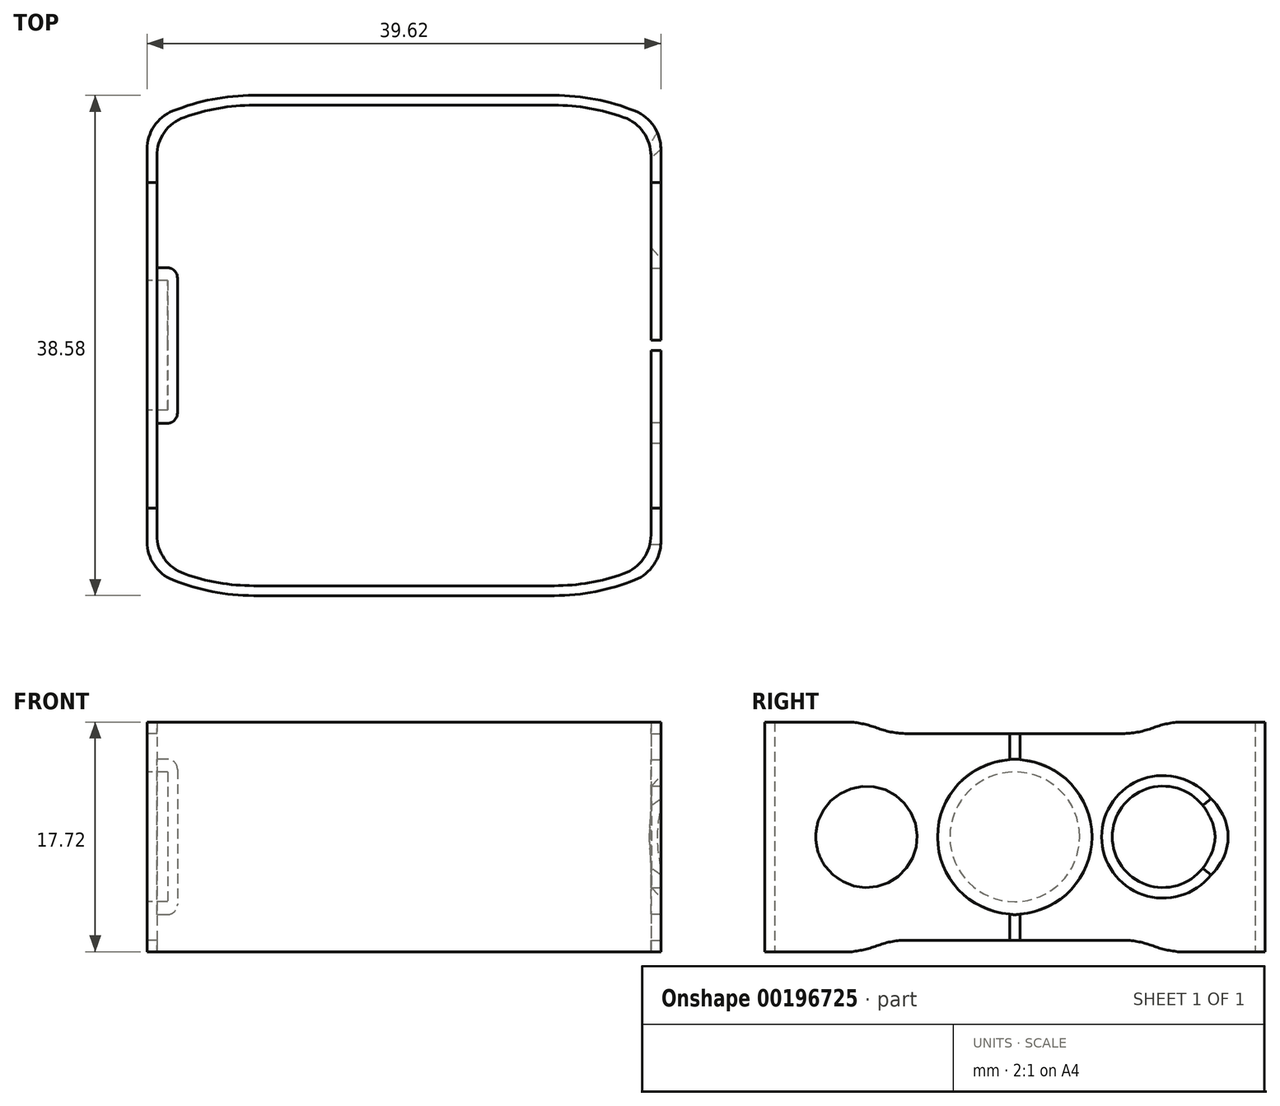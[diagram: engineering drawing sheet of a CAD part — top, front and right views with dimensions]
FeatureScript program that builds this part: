
annotation { "Feature Type Name" : "Feature", "Feature Type Description" : "" }
export const myFeature = defineFeature(function(context is Context, id is Id, definition is map)
    precondition{}
    {
        {
            var Q0;
            Q0=qCreatedBy(makeId("Top.planeOp"),FACE);
            var sketch = newSketch(context, id + "F0", { "sketchPlane" : qUnion([Q0])});
            skLineSegment(sketch, "E0.bottom", {"start": v(19.05, 16.67) * mm, "end": v(-19.05, 16.67) * mm});
            skLineSegment(sketch, "E0.top", {"start": v(19.05, -16.67) * mm, "end": v(-19.05, -16.67) * mm});
            skLineSegment(sketch, "E0.left", {"start": v(19.05, 14.61) * mm, "end": v(19.05, -14.61) * mm});
            skLineSegment(sketch, "E0.right", {"start": v(-19.05, 14.61) * mm, "end": v(-19.05, -14.61) * mm});
            skPoint(sketch, "E0.middle", {"position": v(0, 0) * mm});
            skLineSegment(sketch, "E1", {"start": v(-29.61, 0) * mm, "end": v(26.31, 0) * mm, "construction": true});
            skPoint(sketch, "E1.startSnap0", {"position": v(-19.05, 0) * mm});
            skLineSegment(sketch, "E2", {"start": v(-11.59, 18.53) * mm, "end": v(0, 18.53) * mm});
            skLineSegment(sketch, "E3", {"start": v(0, 18.53) * mm, "end": v(11.59, 18.53) * mm});
            skArc(sketch, "E4", {"start": v(-11.59, 18.53) * mm, "mid": v(-14.3, 18.3) * mm, "end": v(-16.95, 17.6) * mm});
            skArc(sketch, "E5", {"start": v(16.95, 17.6) * mm, "mid": v(14.3, 18.3) * mm, "end": v(11.59, 18.53) * mm});
            skArc(sketch, "E6.MirrorCS", {"start": v(-11.59, -18.53) * mm, "mid": v(-14.3, -18.3) * mm, "end": v(-16.95, -17.6) * mm});
            skLineSegment(sketch, "E7.MirrorCS", {"start": v(-11.59, -18.53) * mm, "end": v(0, -18.53) * mm});
            skLineSegment(sketch, "E8.MirrorCS", {"start": v(0, -18.53) * mm, "end": v(11.59, -18.53) * mm});
            skArc(sketch, "E9.MirrorCS", {"start": v(16.95, -17.6) * mm, "mid": v(14.3, -18.3) * mm, "end": v(11.59, -18.53) * mm});
            skLineSegment(sketch, "E10.0", {"start": v(-11.59, 19.3) * mm, "end": v(0, 19.3) * mm});
            skLineSegment(sketch, "E10.1", {"start": v(0, 19.3) * mm, "end": v(11.59, 19.3) * mm});
            skArc(sketch, "E10.2", {"start": v(-11.59, 19.3) * mm, "mid": v(-14.77, 18.99) * mm, "end": v(-17.83, 18.08) * mm});
            skArc(sketch, "E10.3", {"start": v(17.83, 18.08) * mm, "mid": v(14.77, 18.99) * mm, "end": v(11.59, 19.3) * mm});
            skLineSegment(sketch, "E10.4", {"start": v(19.81, 15.14) * mm, "end": v(19.81, -15.14) * mm});
            skArc(sketch, "E10.5", {"start": v(17.83, -18.08) * mm, "mid": v(14.77, -18.99) * mm, "end": v(11.59, -19.3) * mm});
            skLineSegment(sketch, "E10.6", {"start": v(-19.81, 15.14) * mm, "end": v(-19.81, -15.14) * mm});
            skArc(sketch, "E10.7", {"start": v(-11.59, -19.3) * mm, "mid": v(-14.77, -18.99) * mm, "end": v(-17.83, -18.08) * mm});
            skLineSegment(sketch, "E10.8", {"start": v(-11.59, -19.3) * mm, "end": v(0, -19.3) * mm});
            skLineSegment(sketch, "E10.9", {"start": v(0, -19.3) * mm, "end": v(11.59, -19.3) * mm});
            skPoint(sketch, "E11.visualSharp", {"position": v(-19.05, 16.67) * mm});
            skArc(sketch, "E11.filletArc", {"start": v(-16.95, 17.6) * mm, "mid": v(-18.47, 16.44) * mm, "end": v(-19.05, 14.61) * mm});
            skPoint(sketch, "E12.visualSharp", {"position": v(-19.81, 17.12) * mm});
            skArc(sketch, "E12.filletArc", {"start": v(-17.83, 18.08) * mm, "mid": v(-19.27, 16.91) * mm, "end": v(-19.81, 15.14) * mm});
            skPoint(sketch, "E13.visualSharp", {"position": v(19.05, 16.67) * mm});
            skArc(sketch, "E13.filletArc", {"start": v(19.05, 14.61) * mm, "mid": v(18.47, 16.44) * mm, "end": v(16.95, 17.6) * mm});
            skPoint(sketch, "E14.visualSharp", {"position": v(19.81, 17.12) * mm});
            skArc(sketch, "E14.filletArc", {"start": v(19.81, 15.14) * mm, "mid": v(19.27, 16.91) * mm, "end": v(17.83, 18.08) * mm});
            skPoint(sketch, "E15.visualSharp", {"position": v(19.05, -16.67) * mm});
            skArc(sketch, "E15.filletArc", {"start": v(16.95, -17.6) * mm, "mid": v(18.47, -16.44) * mm, "end": v(19.05, -14.61) * mm});
            skPoint(sketch, "E16.visualSharp", {"position": v(19.81, -17.12) * mm});
            skArc(sketch, "E16.filletArc", {"start": v(17.83, -18.08) * mm, "mid": v(19.27, -16.91) * mm, "end": v(19.81, -15.14) * mm});
            skPoint(sketch, "E17.visualSharp", {"position": v(-19.05, -16.67) * mm});
            skArc(sketch, "E17.filletArc", {"start": v(-19.05, -14.61) * mm, "mid": v(-18.47, -16.44) * mm, "end": v(-16.95, -17.6) * mm});
            skPoint(sketch, "E18.visualSharp", {"position": v(-19.81, -17.12) * mm});
            skArc(sketch, "E18.filletArc", {"start": v(-19.81, -15.14) * mm, "mid": v(-19.27, -16.91) * mm, "end": v(-17.83, -18.08) * mm});
            skSolve(sketch);
        }
        {
            var Q0;
            Q0=makeQuery(id+"F0.imprint","IMPRINT",FACE,{"disambiguationData":[TD([[makeQuery(id+"F0.imprint","IMPRINT",EDGE,{"derivedFrom":sQuery(id+"F0.wireOp",EDGE,"E0.left")}),1.0]])]});
            extrude(context, id + "F1", {"entities" : qUnion([Q0]), "endBound" : BoundingType.SYMMETRIC, "depth" : 17.72 * mm});
        }
        {
            var Q0;
            Q0=makeQuery(id+"F1.opExtrude","SWEPT_FACE",FACE,{"disambiguationData":[OSD([sQuery(id+"F0.wireOp",EDGE,"E10.4")])]});
            var sketch = newSketch(context, id + "F2", { "sketchPlane" : qUnion([Q0])});
            skCircle(sketch, "E19", {"center": v(0, 0) * mm, "radius": 5.95 * mm});
            skLineSegment(sketch, "E20.bottom", {"start": v(0.4, 16.24) * mm, "end": v(-0.4, 16.24) * mm});
            skLineSegment(sketch, "E20.top", {"start": v(0.4, -16.24) * mm, "end": v(-0.4, -16.24) * mm});
            skLineSegment(sketch, "E20.left", {"start": v(0.4, 16.24) * mm, "end": v(0.4, -16.24) * mm});
            skLineSegment(sketch, "E20.right", {"start": v(-0.4, 16.24) * mm, "end": v(-0.4, -16.24) * mm});
            skCircle(sketch, "E21", {"center": v(-11.43, 0) * mm, "radius": 3.9 * mm});
            skLineSegment(sketch, "E22", {"start": v(0, 20.34) * mm, "end": v(0, -24.58) * mm, "construction": true});
            skPoint(sketch, "E22.startSnap0", {"position": v(0, 8.86) * mm});
            skCircle(sketch, "E23.MirrorC", {"center": v(11.43, 0) * mm, "radius": 3.9 * mm});
            skSolve(sketch);
        }
        {
            var Q0;
            Q0=qSketchRegion(id+"F2",true);
            extrude(context, id + "F3", {"entities" : qUnion([Q0]), "operationType" : NewBodyOperationType.REMOVE, "oppositeDirection" : true, "depth" : 25.4 * mm});
        }
        {
            var Q0;
            Q0=qSketchRegion(id+"F2",true);
            extrude(context, id + "F4", {"entities" : qUnion([Q0]), "operationType" : NewBodyOperationType.REMOVE, "oppositeDirection" : true, "depth" : 25.4 * mm});
        }
        {
            var Q0;
            Q0=makeQuery(id+"F3.boolean.opBoolean","COPY",EDGE,{"derivedFrom":makeQuery(id+"F3.opExtrude","CAP_EDGE",EDGE,{"disambiguationData":[OSD([sQuery(id+"F2.wireOp",EDGE,"E21")])],"isStart":true})});
            var Q1;
            Q1=makeQuery(id+"F3.boolean.opBoolean","COPY",EDGE,{"derivedFrom":makeQuery(id+"F3.opExtrude","CAP_EDGE",EDGE,{"disambiguationData":[OSD([sQuery(id+"F2.wireOp",EDGE,"E23.MirrorC")])],"isStart":true})});
            chamfer(context, id + "F5", {"entities" : qUnion([Q0, Q1]), "chamferType" : ChamferType.OFFSET_ANGLE, "width" : 0.71 * mm, "oppositeDirection" : false, "angle" : 49 * degree, "tangentPropagation" : true});
        }
        {
            var Q0;
            Q0=makeQuery(id+"F1.opExtrude","SWEPT_FACE",FACE,{"disambiguationData":[OSD([sQuery(id+"F0.wireOp",EDGE,"E10.6")])]});
            var sketch = newSketch(context, id + "F6", { "sketchPlane" : qUnion([Q0])});
            skCircle(sketch, "E24", {"center": v(0, 0) * mm, "radius": 6 * mm});
            skSolve(sketch);
        }
        {
            var Q0;
            Q0=qSketchRegion(id+"F6",true);
            extrude(context, id + "F7", {"entities" : qUnion([Q0]), "operationType" : NewBodyOperationType.ADD, "oppositeDirection" : true, "depth" : 2.35 * mm});
        }
        {
            var Q0;
            Q0=makeQuery(id+"F1.opExtrude","SWEPT_FACE",FACE,{"disambiguationData":[OSD([sQuery(id+"F0.wireOp",EDGE,"E10.6")])]});
            var sketch = newSketch(context, id + "F8", { "sketchPlane" : qUnion([Q0])});
            skCircle(sketch, "E25", {"center": v(0, 0) * mm, "radius": 5 * mm});
            skSolve(sketch);
        }
        {
            var Q0;
            Q0=qSketchRegion(id+"F8",true);
            extrude(context, id + "F9", {"entities" : qUnion([Q0]), "operationType" : NewBodyOperationType.REMOVE, "oppositeDirection" : true, "depth" : 1.59 * mm});
        }
        {
            var Q0;
            Q0=makeQuery(id+"F9.boolean.opBoolean","COPY",EDGE,{"derivedFrom":makeQuery(id+"F9.opExtrude","CAP_EDGE",EDGE,{"disambiguationData":[OSD([sQuery(id+"F8.wireOp",EDGE,"E25")])],"isStart":true})});
            var Q1;
            Q1=makeQuery(id+"F7.opExtrude","CAP_EDGE",EDGE,{"disambiguationData":[OSD([sQuery(id+"F6.wireOp",EDGE,"E24")])],"isStart":false});
            fillet(context, id + "F10", {"entities" : qUnion([Q0, Q1]), "radius" : 0.8 * mm, "tangentPropagation" : true, "allowEdgeOverflow" : false});
        }
        {
            var Q0;
            Q0=makeQuery(id+"F1.opExtrude","SWEPT_FACE",FACE,{"disambiguationData":[OSD([sQuery(id+"F0.wireOp",EDGE,"E10.6")])]});
            var sketch = newSketch(context, id + "F11", { "sketchPlane" : qUnion([Q0])});
            skLineSegment(sketch, "E26", {"start": v(-8.32, 7.97) * mm, "end": v(8.32, 7.97) * mm});
            skLineSegment(sketch, "E27", {"start": v(0, 3.4) * mm, "end": v(0, -3) * mm, "construction": true});
            skLineSegment(sketch, "E28", {"start": v(-2.44, 0) * mm, "end": v(2.9, 0) * mm, "construction": true});
            skArc(sketch, "E29", {"start": v(-10.53, 8.37) * mm, "mid": v(-9.44, 8.07) * mm, "end": v(-8.32, 7.97) * mm});
            skArc(sketch, "E30", {"start": v(-10.53, 8.37) * mm, "mid": v(-12.05, 8.78) * mm, "end": v(-13.62, 8.92) * mm});
            skArc(sketch, "E31.MirrorCS", {"start": v(10.53, 8.37) * mm, "mid": v(12.05, 8.78) * mm, "end": v(13.62, 8.92) * mm});
            skArc(sketch, "E32.MirrorCS", {"start": v(10.53, 8.37) * mm, "mid": v(9.44, 8.07) * mm, "end": v(8.32, 7.97) * mm});
            skLineSegment(sketch, "E33", {"start": v(-13.62, 8.92) * mm, "end": v(13.62, 8.92) * mm});
            skLineSegment(sketch, "E34", {"start": v(-13.62, 8.92) * mm, "end": v(-24.45, 8.92) * mm, "construction": true});
            skLineSegment(sketch, "E35.MirrorCS", {"start": v(-8.32, -7.97) * mm, "end": v(8.32, -7.97) * mm});
            skLineSegment(sketch, "E36.MirrorCS", {"start": v(-13.62, -8.92) * mm, "end": v(-24.45, -8.92) * mm, "construction": true});
            skArc(sketch, "E37.MirrorCS", {"start": v(-10.53, -8.37) * mm, "mid": v(-9.44, -8.07) * mm, "end": v(-8.32, -7.97) * mm});
            skLineSegment(sketch, "E38.MirrorCS", {"start": v(-13.62, -8.92) * mm, "end": v(13.62, -8.92) * mm});
            skArc(sketch, "E39.MirrorCS", {"start": v(10.53, -8.37) * mm, "mid": v(12.05, -8.78) * mm, "end": v(13.62, -8.92) * mm});
            skArc(sketch, "E40.MirrorCS", {"start": v(10.53, -8.37) * mm, "mid": v(9.44, -8.07) * mm, "end": v(8.32, -7.97) * mm});
            skArc(sketch, "E41.MirrorCS", {"start": v(-10.53, -8.37) * mm, "mid": v(-12.05, -8.78) * mm, "end": v(-13.62, -8.92) * mm});
            skSolve(sketch);
        }
        {
            var Q0;
            Q0 = qSketchRegion(id + "F11", true);
            extrude(context, id + "F12", {"entities" : qUnion([Q0]), "operationType" : NewBodyOperationType.REMOVE, "endBound" : BoundingType.THROUGH_ALL, "oppositeDirection" : true, "depth" : 25.4 * mm});
        }
    });
